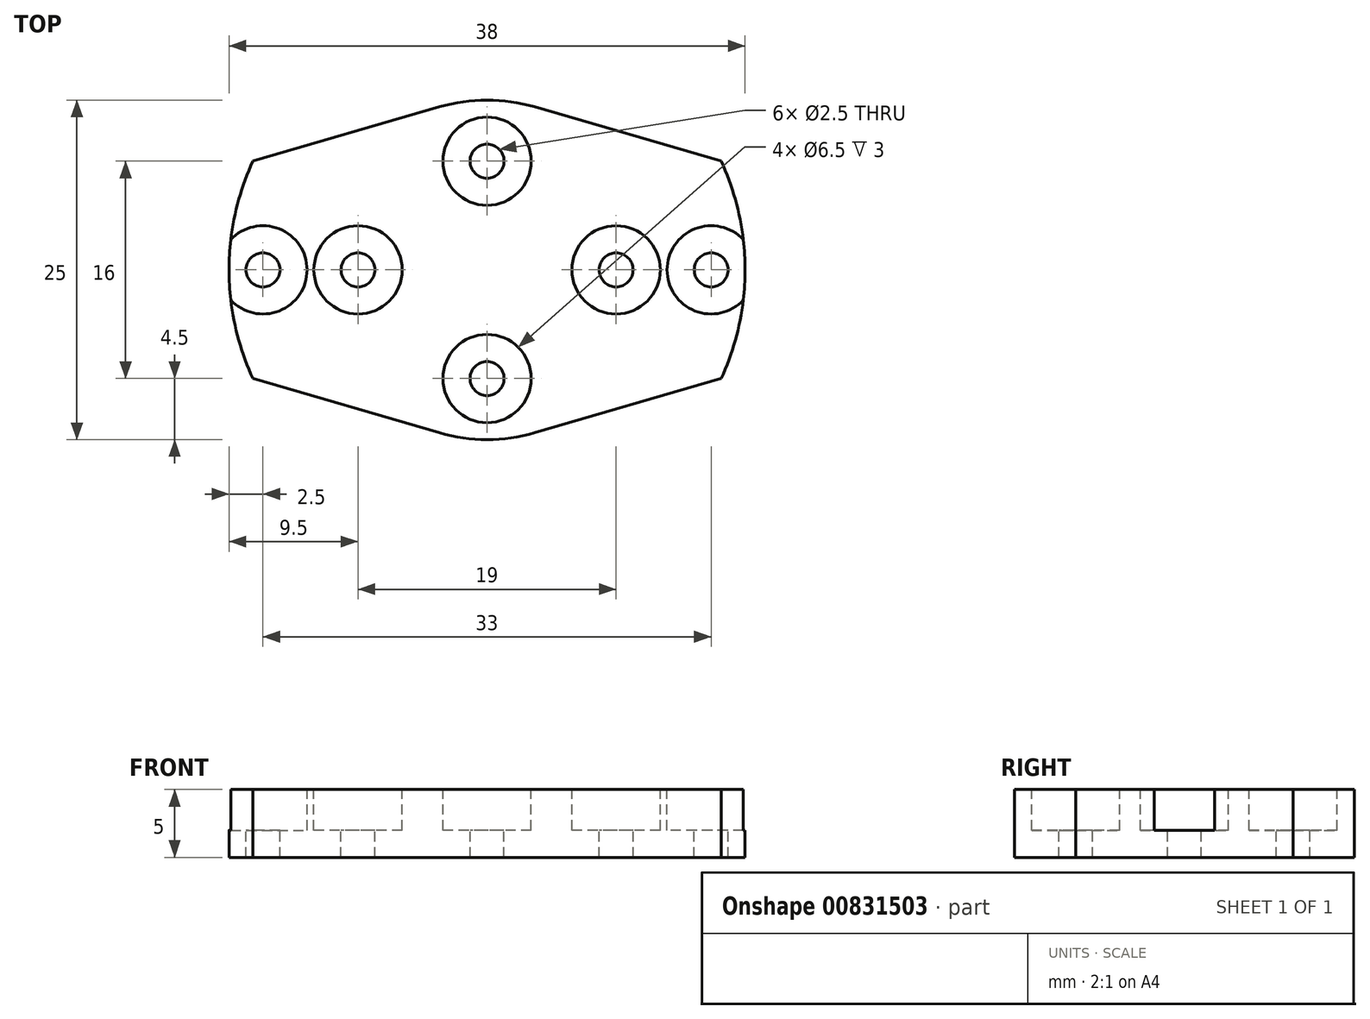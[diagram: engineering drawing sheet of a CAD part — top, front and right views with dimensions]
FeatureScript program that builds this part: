
annotation { "Feature Type Name" : "Feature", "Feature Type Description" : "" }
export const myFeature = defineFeature(function(context is Context, id is Id, definition is map)
    precondition{}
    {
        {
            var Q0;
            Q0=qCreatedBy(makeId("Top.planeOp"),FACE);
            var sketch = newSketch(context, id + "F0", { "sketchPlane" : qUnion([Q0])});
            skCircle(sketch, "E0", {"center": v(0, 0) * mm, "radius": 12.5 * mm, "construction": true});
            skCircle(sketch, "E1", {"center": v(0, 0) * mm, "radius": 19 * mm, "construction": true});
            skLineSegment(sketch, "E2", {"start": v(-17.23, 8) * mm, "end": v(-3.5, 12) * mm});
            skLineSegment(sketch, "E3", {"start": v(0, 0) * mm, "end": v(-19, 0) * mm, "construction": true});
            skLineSegment(sketch, "E4", {"start": v(0, 0) * mm, "end": v(0, 19) * mm, "construction": true});
            skLineSegment(sketch, "E5.MirrorCS", {"start": v(-17.23, -8) * mm, "end": v(-3.5, -12) * mm});
            skLineSegment(sketch, "E6.MirrorCS", {"start": v(17.23, 8) * mm, "end": v(3.5, 12) * mm});
            skLineSegment(sketch, "E7.MirrorCS", {"start": v(17.23, -8) * mm, "end": v(3.5, -12) * mm});
            skArc(sketch, "E8", {"start": v(-3.5, 12) * mm, "mid": v(0, 12.5) * mm, "end": v(3.5, 12) * mm});
            skArc(sketch, "E9", {"start": v(-3.5, -12) * mm, "mid": v(0, -12.5) * mm, "end": v(3.5, -12) * mm});
            skArc(sketch, "E10", {"start": v(-17.23, 8) * mm, "mid": v(-19, 0) * mm, "end": v(-17.23, -8) * mm});
            skArc(sketch, "E11", {"start": v(17.23, 8) * mm, "mid": v(19, 0) * mm, "end": v(17.23, -8) * mm});
            skSolve(sketch);
        }
        {
            var Q0;
            Q0 = qSketchRegion(id + "F0", true);
            extrude(context, id + "F1", {"entities" : qUnion([Q0]), "depth" : 5 * mm, "offsetDistance" : 25 * mm});
        }
        {
            var Q0;
            Q0=makeQuery(id+"F1.opExtrude","CAP_FACE",FACE,{"disambiguationData":[OSD([sQuery(id+"F0.wireOp",EDGE,"E2"),sQuery(id+"F0.wireOp",EDGE,"E5.MirrorCS"),sQuery(id+"F0.wireOp",EDGE,"E6.MirrorCS"),sQuery(id+"F0.wireOp",EDGE,"E7.MirrorCS"),sQuery(id+"F0.wireOp",EDGE,"E8"),sQuery(id+"F0.wireOp",EDGE,"E9"),sQuery(id+"F0.wireOp",EDGE,"E10"),sQuery(id+"F0.wireOp",EDGE,"E11")])],"isStart":false});
            var sketch = newSketch(context, id + "F2", { "sketchPlane" : qUnion([Q0])});
            skLineSegment(sketch, "E12", {"start": v(-9.5, 0) * mm, "end": v(9.5, 0) * mm, "construction": true});
            skLineSegment(sketch, "E13", {"start": v(0, 8) * mm, "end": v(0, -8) * mm, "construction": true});
            skLineSegment(sketch, "E14", {"start": v(-16.5, 0) * mm, "end": v(16.5, 0) * mm, "construction": true});
            skSolve(sketch);
        }
        {
            var Q0;
            Q0=sQuery(id+"F2.wireOp",VERTEX,"E12.start");
            var Q1;
            Q1=sQuery(id+"F2.wireOp",VERTEX,"E13.start");
            var Q2;
            Q2=sQuery(id+"F2.wireOp",VERTEX,"E12.end");
            var Q3;
            Q3=sQuery(id+"F2.wireOp",VERTEX,"E13.end");
            var Q4;
            Q4=sQuery(id+"F2.wireOp",VERTEX,"E14.start");
            var Q5;
            Q5=sQuery(id+"F2.wireOp",VERTEX,"E14.end");
            var Q6;
            Q6=makeQuery(id+"F1.opExtrude","SWEPT_BODY",BODY,{"disambiguationData":[OSD([sQuery(id+"F0.wireOp",EDGE,"E2"),sQuery(id+"F0.wireOp",EDGE,"E5.MirrorCS"),sQuery(id+"F0.wireOp",EDGE,"E6.MirrorCS"),sQuery(id+"F0.wireOp",EDGE,"E7.MirrorCS"),sQuery(id+"F0.wireOp",EDGE,"E8"),sQuery(id+"F0.wireOp",EDGE,"E9"),sQuery(id+"F0.wireOp",EDGE,"E10"),sQuery(id+"F0.wireOp",EDGE,"E11")])]});
            hole(context, id + "F3", {"style" : HoleStyle.C_BORE, "endStyle" : HoleEndStyle.THROUGH, "standardTappedOrClearance" : lookupTablePath({ "standard" : "ISO", "engagement" : "75%", "pitch" : "0.5 mm", "size" : "M3", "type" : "Tapped" }), "standardBlindInLast" : lookupTablePath({ "standard" : "ISO", "engagement" : "75%", "pitch" : "0.5 mm", "size" : "M3", "type" : "Tapped" }), "holeDiameter" : 2.5 * mm, "cBoreDiameter" : 6.5 * mm, "cBoreDepth" : 3 * mm, "majorDiameter" : 3 * mm, "showTappedDepth" : true, "isTappedThrough" : true, "tappedDepth" : 5 * mm, "tapClearance" : 3, "startFromSketch" : true, "locations" : qUnion([Q0, Q1, Q2, Q3, Q4, Q5]), "scope" : qUnion([Q6])});
        }
    });
